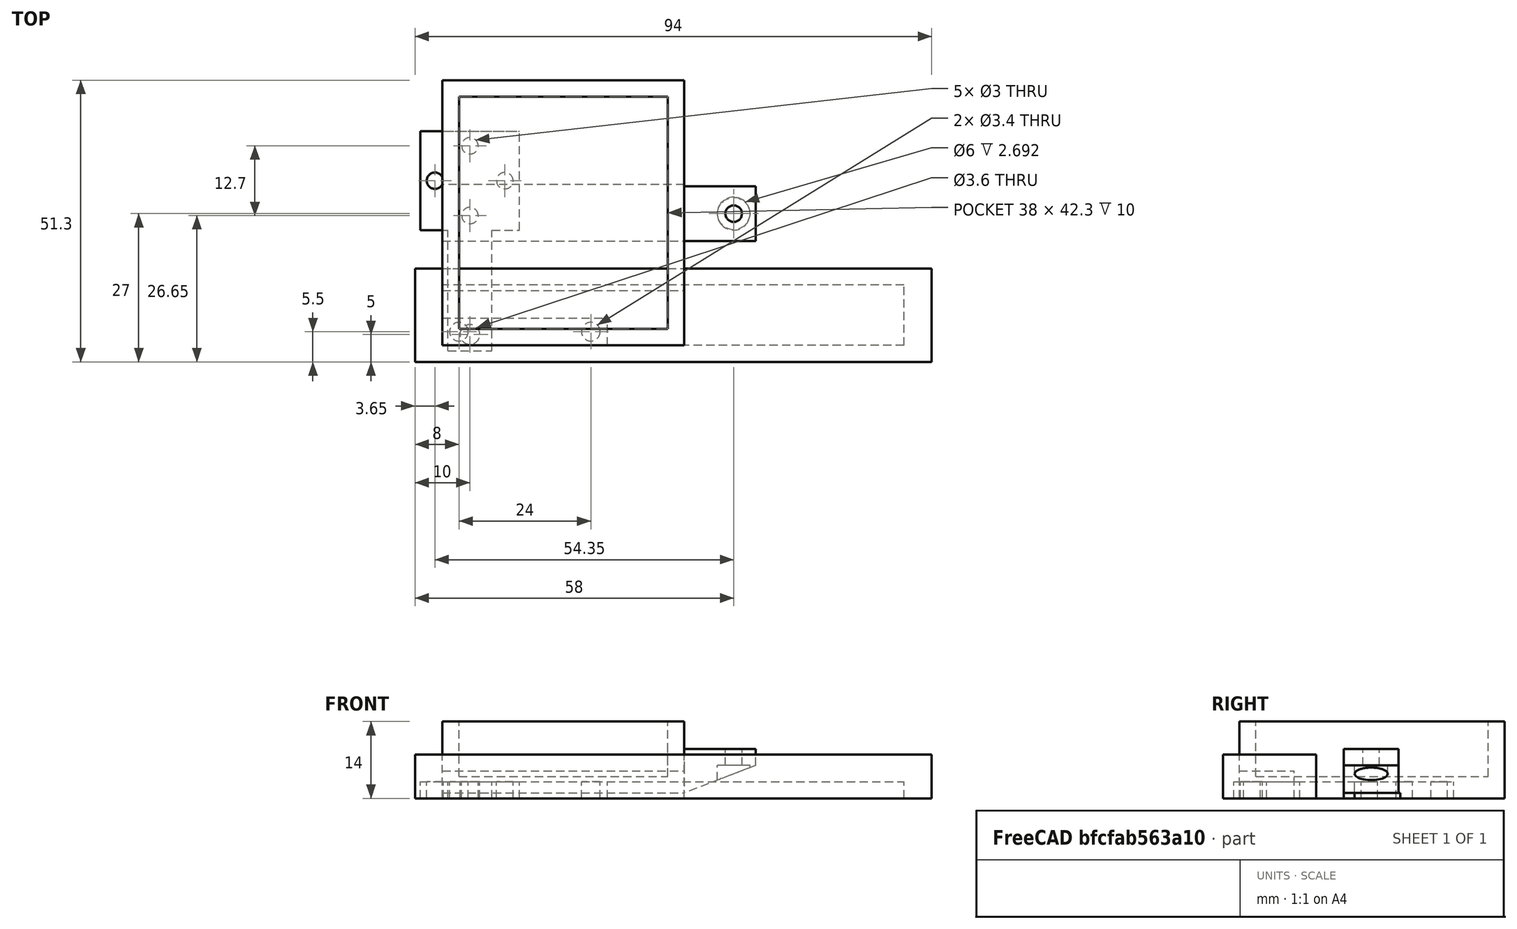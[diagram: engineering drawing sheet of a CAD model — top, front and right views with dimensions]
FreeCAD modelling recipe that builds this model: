
FCSTD DOCUMENT  (FreeCAD 0.18R16093 (Git))
Label: Slider
License: All rights reserved
LicenseURL: http://en.wikipedia.org/wiki/All_rights_reserved
objects: Part::Cut×13, Part::Box×10, Part::Cylinder×10, Part::MultiFuse×3, Part::Wedge×1
note: 37 computed .brp shape members not serialized (recipe doc carries the construction recipe); baked Part::Feature solids carry a one-line shape summary decoded from their .brp

FEATURE [Part::Box] Box  label="Tray"
  AttacherType = Attacher::AttachEngine3D
  Height = 14
  Length = 44
  Width = 48.3
FEATURE [Part::Box] Box001  label="Tray_Negative"
  AttacherType = Attacher::AttachEngine3D
  Height = 10
  Length = 38
  Placement = pos=(3,3,4) rot=(0,0,1;0rad)
  Width = 42.3
FEATURE [Part::Cut] Cut
  Base = -> Box
  Tool = -> Box001
FEATURE [Part::Box] Box002  label="SlideSection"
  AttacherType = Attacher::AttachEngine3D
  Height = 5
  Length = 44
  Placement = pos=(0,19,-4) rot=(0,0,1;0rad)
  Width = 10.3
FEATURE [Part::Box] Box003  label="SlideSection001"
  AttacherType = Attacher::AttachEngine3D
  Height = 5
  Length = 44
  Width = 10
FEATURE [Part::Cut] Cut001  label="MainTray"
  Base = -> Cut
  Tool = -> Box002
FEATURE [Part::Box] Box004  label="SlideModule"
  AttacherType = Attacher::AttachEngine3D
  Height = 8
  Length = 94
  Placement = pos=(-5,-3,0) rot=(0,0,1;0rad)
  Width = 17
FEATURE [Part::Box] Box005  label="SlideModuleNegative"
  AttacherType = Attacher::AttachEngine3D
  Height = 5
  Length = 84
  Placement = pos=(0,0,-2) rot=(0,0,1;0rad)
  Width = 11
FEATURE [Part::Cut] Cut002  label="SlidingModule"
  Base = -> Box004
  Tool = -> Box005
FEATURE [Part::Cylinder] Cylinder
  Angle = 360
  AttacherType = Attacher::AttachEngine3D
  Height = 10
  Placement = pos=(53,24,0) rot=(0,0,1;0rad)
  Radius = 1.5
FEATURE [Part::Box] Box007  label="SliderConnect001"
  AttacherType = Attacher::AttachEngine3D
  Height = 3
  Length = 16
  Placement = pos=(41,19,6) rot=(0,0,1;0rad)
  Width = 10
FEATURE [Part::Cut] Cut003  label="SlideConnector"
  Base = -> Box007
  Tool = -> Cylinder
FEATURE [Part::Wedge] Wedge  label="SlideConnectorSupport"
  AttacherType = Attacher::AttachEngine3D
  Placement = pos=(44,19,6) rot=(-1,0,0;1.5708rad)
  X2max = 0
  X2min = 0
  Xmax = 13
  Xmin = 0
  Ymax = 5
  Ymin = 0
  Z2max = 10
  Z2min = 0
  Zmax = 10
  Zmin = 0
FEATURE [Part::MultiFuse] Fusion
  Shapes = -> [Cut003,Wedge]
FEATURE [Part::MultiFuse] Fusion001  label="SliderTray"
  Shapes = -> [Fusion,Cut001]
FEATURE [Part::Cylinder] Cylinder001
  Angle = 360
  AttacherType = Attacher::AttachEngine3D
  Height = 10
  Placement = pos=(53,24,0) rot=(0,0,1;0rad)
  Radius = 1.5
FEATURE [Part::Cut] Cut004
  Base = -> Fusion001
  Tool = -> Cylinder001
FEATURE [Part::Cylinder] Cylinder002
  Angle = 360
  AttacherType = Attacher::AttachEngine3D
  Height = 10
  Placement = pos=(53,24,-4) rot=(0,0,1;0rad)
  Radius = 3
FEATURE [Part::Cut] Cut005  label="SildeFullTray"
  Base = -> Cut004
  Tool = -> Cylinder002
FEATURE [Part::Box] Box008  label="SliderArm"
  AttacherType = Attacher::AttachEngine3D
  Height = 3
  Length = 30
  Width = 5
FEATURE [Part::Cylinder] Cylinder003
  Angle = 360
  AttacherType = Attacher::AttachEngine3D
  Height = 10
  Placement = pos=(3,2.5,0) rot=(0,0,1;0rad)
  Radius = 1.7
FEATURE [Part::Cylinder] Cylinder004
  Angle = 360
  AttacherType = Attacher::AttachEngine3D
  Height = 10
  Placement = pos=(27,2.5,0) rot=(0,0,1;0rad)
  Radius = 1.7
FEATURE [Part::Cut] Cut006
  Base = -> Box008
  Tool = -> Cylinder003
FEATURE [Part::Cut] Cut007  label="SlideArm"
  Base = -> Cut006
  Tool = -> Cylinder004
FEATURE [Part::Box] Box009  label="SlideMotorArm"
  AttacherType = Attacher::AttachEngine3D
  Height = 3
  Length = 18
  Placement = pos=(-4,21,0) rot=(0,0,1;0rad)
  Width = 18
FEATURE [Part::Cylinder] Cylinder006
  Angle = 360
  AttacherType = Attacher::AttachEngine3D
  Height = 10
  Placement = pos=(5,36.35,0) rot=(0,0,1;0rad)
  Radius = 1.5
FEATURE [Part::Cylinder] Cylinder007
  Angle = 360
  AttacherType = Attacher::AttachEngine3D
  Height = 10
  Placement = pos=(11.35,30,0) rot=(0,0,1;0rad)
  Radius = 1.5
FEATURE [Part::Cylinder] Cylinder008
  Angle = 360
  AttacherType = Attacher::AttachEngine3D
  Height = 10
  Placement = pos=(-1.35,30,0) rot=(0,0,1;0rad)
  Radius = 1.5
FEATURE [Part::Cylinder] Cylinder009
  Angle = 360
  AttacherType = Attacher::AttachEngine3D
  Height = 10
  Placement = pos=(5,23.65,0) rot=(0,0,1;0rad)
  Radius = 1.5
FEATURE [Part::Cylinder] Cylinder005
  Angle = 360
  AttacherType = Attacher::AttachEngine3D
  Height = 10
  Placement = pos=(5,2,0) rot=(0,0,1;0rad)
  Radius = 1.8
FEATURE [Part::Box] Box010  label="SlideMotorArmExt"
  AttacherType = Attacher::AttachEngine3D
  Height = 3
  Length = 8
  Placement = pos=(1,-1,0) rot=(0,0,1;0rad)
  Width = 22
FEATURE [Part::Cut] Cut008
  Base = -> Box009
  Tool = -> Cylinder006
FEATURE [Part::Cut] Cut009
  Base = -> Cut008
  Tool = -> Cylinder007
FEATURE [Part::Cut] Cut010
  Base = -> Cut009
  Tool = -> Cylinder008
FEATURE [Part::Cut] Cut011
  Base = -> Cut010
  Tool = -> Cylinder009
FEATURE [Part::Cut] Cut012
  Base = -> Box010
  Tool = -> Cylinder005
FEATURE [Part::MultiFuse] Fusion002  label="SlideMotorArmExtension"
  Shapes = -> [Cut011,Cut012]
